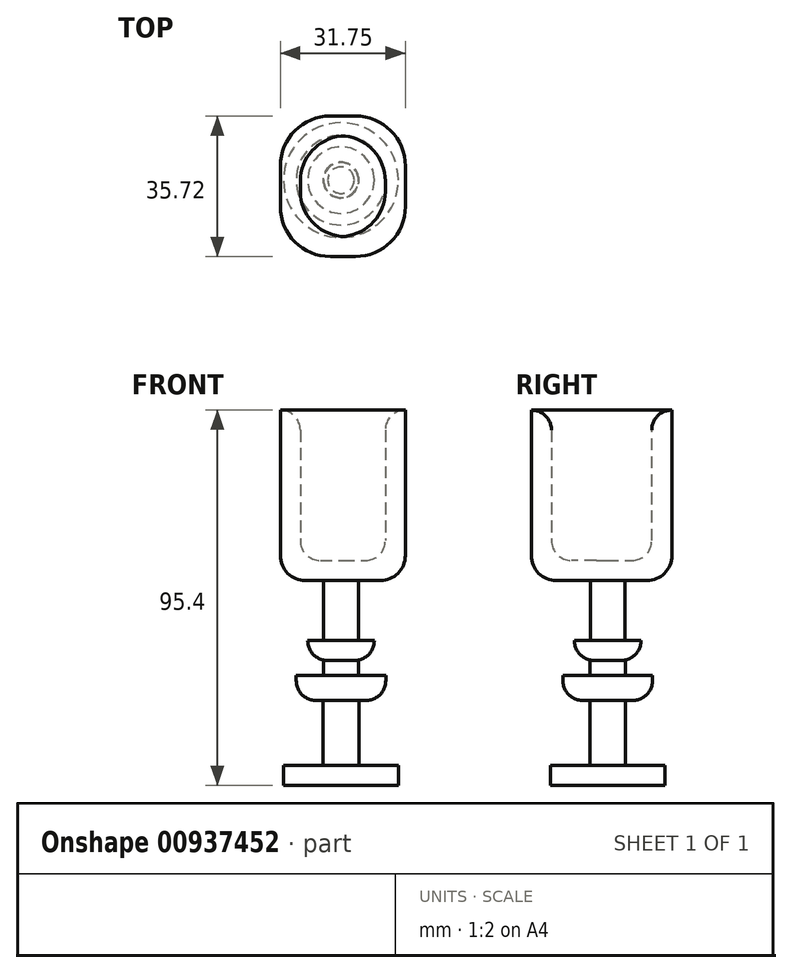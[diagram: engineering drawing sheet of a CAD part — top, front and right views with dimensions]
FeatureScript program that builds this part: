
annotation { "Feature Type Name" : "Feature", "Feature Type Description" : "" }
export const myFeature = defineFeature(function(context is Context, id is Id, definition is map)
    precondition{}
    {
        {
            var Q0;
            Q0=qCreatedBy(makeId("Right.planeOp"),FACE);
            var sketch = newSketch(context, id + "F0", { "sketchPlane" : qUnion([Q0])});
            skLineSegment(sketch, "E0.bottom", {"start": v(-15.73, 59.27) * mm, "end": v(19.99, 59.27) * mm});
            skLineSegment(sketch, "E0.top", {"start": v(-15.73, 15.94) * mm, "end": v(19.99, 15.94) * mm});
            skLineSegment(sketch, "E0.left", {"start": v(-15.73, 59.27) * mm, "end": v(-15.73, 15.94) * mm});
            skLineSegment(sketch, "E0.right", {"start": v(19.99, 59.27) * mm, "end": v(19.99, 15.94) * mm});
            skPoint(sketch, "E0.middle", {"position": v(2.13, 37.6) * mm});
            skSolve(sketch);
        }
        {
            var Q0;
            Q0 = qSketchRegion(id + "F0", true);
            extrude(context, id + "F1", {"entities" : qUnion([Q0]), "depth" : 31.75 * mm, "offsetDistance" : 25.4 * mm});
        }
        {
            var Q0;
            Q0=makeQuery(id+"F1.opExtrude","SWEPT_FACE",FACE,{"disambiguationData":[OSD([sQuery(id+"F0.wireOp",EDGE,"E0.bottom")])]});
            shell(context, id + "F2", {"entities" : qUnion([Q0]), "thickness" : 5.08 * mm});
        }
        {
            var Q0;
            Q0=makeQuery(id+"F1.opExtrude","CAP_EDGE",EDGE,{"disambiguationData":[OSD([sQuery(id+"F0.wireOp",EDGE,"E0.left")])],"isStart":true});
            var Q1;
            Q1=makeQuery(id+"F1.opExtrude","CAP_EDGE",EDGE,{"disambiguationData":[OSD([sQuery(id+"F0.wireOp",EDGE,"E0.left")])],"isStart":false});
            var Q2;
            Q2=makeQuery(id+"F1.opExtrude","CAP_EDGE",EDGE,{"disambiguationData":[OSD([sQuery(id+"F0.wireOp",EDGE,"E0.right")])],"isStart":false});
            var Q3;
            Q3=makeQuery(id+"F1.opExtrude","CAP_EDGE",EDGE,{"disambiguationData":[OSD([sQuery(id+"F0.wireOp",EDGE,"E0.right")])],"isStart":true});
            fillet(context, id + "F3", {"entities" : qUnion([Q0, Q1, Q2, Q3]), "radius" : 12.7 * mm, "tangentPropagation" : true, "allowEdgeOverflow" : false});
        }
        {
            var Q0;
            {var subQ0=sQuery(id+"F0.wireOp",EDGE,"E0.left");Q0=makeQuery(id+"F2.opShell","OFFSET_EDGE",EDGE,{"disambiguationData":[OSD([subQ0]),TDD([makeQuery(id+"F1.opExtrude","CAP_EDGE",EDGE,{"disambiguationData":[OSD([subQ0])],"isStart":true})])]});}
            var Q1;
            {var subQ0=sQuery(id+"F0.wireOp",EDGE,"E0.right");Q1=makeQuery(id+"F2.opShell","OFFSET_EDGE",EDGE,{"disambiguationData":[OSD([subQ0]),TDD([makeQuery(id+"F1.opExtrude","CAP_EDGE",EDGE,{"disambiguationData":[OSD([subQ0])],"isStart":true})])]});}
            var Q2;
            {var subQ0=sQuery(id+"F0.wireOp",EDGE,"E0.right");Q2=makeQuery(id+"F2.opShell","OFFSET_EDGE",EDGE,{"disambiguationData":[OSD([subQ0]),TDD([makeQuery(id+"F1.opExtrude","CAP_EDGE",EDGE,{"disambiguationData":[OSD([subQ0])],"isStart":false})])]});}
            var Q3;
            {var subQ0=sQuery(id+"F0.wireOp",EDGE,"E0.left");Q3=makeQuery(id+"F2.opShell","OFFSET_EDGE",EDGE,{"disambiguationData":[OSD([subQ0]),TDD([makeQuery(id+"F1.opExtrude","CAP_EDGE",EDGE,{"disambiguationData":[OSD([subQ0])],"isStart":false})])]});}
            fillet(context, id + "F4", {"entities" : qUnion([Q0, Q1, Q2, Q3]), "radius" : 11.43 * mm, "tangentPropagation" : true, "allowEdgeOverflow" : false});
        }
        {
            var Q0;
            Q0=makeQuery(id+"F1.opExtrude","SWEPT_EDGE",EDGE,{"disambiguationData":[OSD([sQuery(id+"F0.wireOp",EDGE,"E0.top"),sQuery(id+"F0.wireOp",EDGE,"E0.left")])]});
            var Q1;
            Q1=makeQuery(id+"F3.opFillet","BLEND_EDGE",EDGE,{"blendedFrom":[makeQuery(id+"F1.opExtrude","CAP_EDGE",EDGE,{"disambiguationData":[OSD([sQuery(id+"F0.wireOp",EDGE,"E0.left")])],"isStart":true}),makeQuery(id+"F1.opExtrude","SWEPT_FACE",FACE,{"disambiguationData":[OSD([sQuery(id+"F0.wireOp",EDGE,"E0.top")])]})],"blendedInto":[makeQuery(id+"F1.opExtrude","SWEPT_FACE",FACE,{"disambiguationData":[OSD([sQuery(id+"F0.wireOp",EDGE,"E0.top")])]})]});
            var Q2;
            Q2=makeQuery(id+"F1.opExtrude","CAP_EDGE",EDGE,{"disambiguationData":[OSD([sQuery(id+"F0.wireOp",EDGE,"E0.top")])],"isStart":true});
            var Q3;
            Q3=makeQuery(id+"F3.opFillet","BLEND_EDGE",EDGE,{"blendedFrom":[makeQuery(id+"F1.opExtrude","CAP_EDGE",EDGE,{"disambiguationData":[OSD([sQuery(id+"F0.wireOp",EDGE,"E0.right")])],"isStart":true}),makeQuery(id+"F1.opExtrude","SWEPT_FACE",FACE,{"disambiguationData":[OSD([sQuery(id+"F0.wireOp",EDGE,"E0.top")])]})],"blendedInto":[makeQuery(id+"F1.opExtrude","SWEPT_FACE",FACE,{"disambiguationData":[OSD([sQuery(id+"F0.wireOp",EDGE,"E0.top")])]})]});
            var Q4;
            Q4=makeQuery(id+"F1.opExtrude","SWEPT_EDGE",EDGE,{"disambiguationData":[OSD([sQuery(id+"F0.wireOp",EDGE,"E0.top"),sQuery(id+"F0.wireOp",EDGE,"E0.right")])]});
            var Q5;
            Q5=makeQuery(id+"F3.opFillet","BLEND_EDGE",EDGE,{"blendedFrom":[makeQuery(id+"F1.opExtrude","CAP_EDGE",EDGE,{"disambiguationData":[OSD([sQuery(id+"F0.wireOp",EDGE,"E0.right")])],"isStart":false}),makeQuery(id+"F1.opExtrude","SWEPT_FACE",FACE,{"disambiguationData":[OSD([sQuery(id+"F0.wireOp",EDGE,"E0.top")])]})],"blendedInto":[makeQuery(id+"F1.opExtrude","SWEPT_FACE",FACE,{"disambiguationData":[OSD([sQuery(id+"F0.wireOp",EDGE,"E0.top")])]})]});
            var Q6;
            Q6=makeQuery(id+"F1.opExtrude","CAP_EDGE",EDGE,{"disambiguationData":[OSD([sQuery(id+"F0.wireOp",EDGE,"E0.top")])],"isStart":false});
            var Q7;
            Q7=makeQuery(id+"F3.opFillet","BLEND_EDGE",EDGE,{"blendedFrom":[makeQuery(id+"F1.opExtrude","CAP_EDGE",EDGE,{"disambiguationData":[OSD([sQuery(id+"F0.wireOp",EDGE,"E0.left")])],"isStart":false}),makeQuery(id+"F1.opExtrude","SWEPT_FACE",FACE,{"disambiguationData":[OSD([sQuery(id+"F0.wireOp",EDGE,"E0.top")])]})],"blendedInto":[makeQuery(id+"F1.opExtrude","SWEPT_FACE",FACE,{"disambiguationData":[OSD([sQuery(id+"F0.wireOp",EDGE,"E0.top")])]})]});
            fillet(context, id + "F5", {"entities" : qUnion([Q0, Q1, Q2, Q3, Q4, Q5, Q6, Q7]), "radius" : 6.35 * mm, "tangentPropagation" : true, "allowEdgeOverflow" : false});
        }
        {
            var Q0;
            {var subQ0=sQuery(id+"F0.wireOp",EDGE,"E0.right");Q0=makeQuery(id+"F4.opFillet","BLEND_FACE",FACE,{"disambiguationData":[OSD([subQ0]),TDD([makeQuery(id+"F2.opShell","OFFSET_EDGE",EDGE,{"disambiguationData":[OSD([subQ0]),TDD([makeQuery(id+"F1.opExtrude","CAP_EDGE",EDGE,{"disambiguationData":[OSD([subQ0])],"isStart":false})])]})])]});}
            var Q1;
            {var subQ0=sQuery(id+"F0.wireOp",EDGE,"E0.left");Q1=makeQuery(id+"F4.opFillet","BLEND_FACE",FACE,{"disambiguationData":[OSD([subQ0]),TDD([makeQuery(id+"F2.opShell","OFFSET_EDGE",EDGE,{"disambiguationData":[OSD([subQ0]),TDD([makeQuery(id+"F1.opExtrude","CAP_EDGE",EDGE,{"disambiguationData":[OSD([subQ0])],"isStart":false})])]})])]});}
            var Q2;
            {var subQ0=sQuery(id+"F0.wireOp",EDGE,"E0.right");Q2=makeQuery(id+"F4.opFillet","BLEND_FACE",FACE,{"disambiguationData":[OSD([subQ0]),TDD([makeQuery(id+"F2.opShell","OFFSET_EDGE",EDGE,{"disambiguationData":[OSD([subQ0]),TDD([makeQuery(id+"F1.opExtrude","CAP_EDGE",EDGE,{"disambiguationData":[OSD([subQ0])],"isStart":true})])]})])]});}
            var Q3;
            {var subQ0=sQuery(id+"F0.wireOp",EDGE,"E0.left");Q3=makeQuery(id+"F4.opFillet","BLEND_FACE",FACE,{"disambiguationData":[OSD([subQ0]),TDD([makeQuery(id+"F2.opShell","OFFSET_EDGE",EDGE,{"disambiguationData":[OSD([subQ0]),TDD([makeQuery(id+"F1.opExtrude","CAP_EDGE",EDGE,{"disambiguationData":[OSD([subQ0])],"isStart":true})])]})])]});}
            fillet(context, id + "F6", {"entities" : qUnion([Q0, Q1, Q2, Q3]), "radius" : 5.08 * mm, "tangentPropagation" : true, "allowEdgeOverflow" : false});
        }
        {
            var Q0;
            Q0=makeQuery(id+"F1.opExtrude","SWEPT_FACE",FACE,{"disambiguationData":[OSD([sQuery(id+"F0.wireOp",EDGE,"E0.top")])]});
            var sketch = newSketch(context, id + "F7", { "sketchPlane" : qUnion([Q0])});
            skCircle(sketch, "E1", {"center": v(15.41, -3.7) * mm, "radius": 4.43 * mm});
            skSolve(sketch);
        }
        {
            var Q0;
            Q0 = qSketchRegion(id + "F7", true);
            extrude(context, id + "F8", {"entities" : qUnion([Q0]), "operationType" : NewBodyOperationType.ADD, "depth" : 15.24 * mm, "offsetDistance" : 25.4 * mm});
        }
        {
            var Q0;
            Q0=makeQuery(id+"F8.opExtrude","CAP_FACE",FACE,{"disambiguationData":[OSD([sQuery(id+"F7.wireOp",EDGE,"E1")])],"isStart":false});
            var sketch = newSketch(context, id + "F9", { "sketchPlane" : qUnion([Q0])});
            skCircle(sketch, "E2", {"center": v(15.41, -3.7) * mm, "radius": 8.45 * mm});
            skSolve(sketch);
        }
        {
            var Q0;
            Q0 = qSketchRegion(id + "F9", true);
            extrude(context, id + "F10", {"entities" : qUnion([Q0]), "operationType" : NewBodyOperationType.ADD, "depth" : 5.08 * mm, "offsetDistance" : 25.4 * mm});
        }
        {
            var Q0;
            Q0=makeQuery(id+"F10.opExtrude","CAP_EDGE",EDGE,{"disambiguationData":[OSD([sQuery(id+"F9.wireOp",EDGE,"E2")])],"isStart":false});
            fillet(context, id + "F11", {"entities" : qUnion([Q0]), "radius" : 5.08 * mm, "tangentPropagation" : true, "allowEdgeOverflow" : false});
        }
        {
            var Q0;
            Q0=makeQuery(id+"F10.opExtrude","CAP_FACE",FACE,{"disambiguationData":[OSD([sQuery(id+"F9.wireOp",EDGE,"E2")])],"isStart":false});
            var sketch = newSketch(context, id + "F12", { "sketchPlane" : qUnion([Q0])});
            skCircle(sketch, "E3", {"center": v(15.41, -3.7) * mm, "radius": 4.45 * mm});
            skSolve(sketch);
        }
        {
            var Q0;
            Q0 = qSketchRegion(id + "F12", true);
            extrude(context, id + "F13", {"entities" : qUnion([Q0]), "operationType" : NewBodyOperationType.ADD, "depth" : 3.8 * mm, "offsetDistance" : 25.4 * mm});
        }
        {
            var Q0;
            Q0=makeQuery(id+"F13.opExtrude","CAP_FACE",FACE,{"disambiguationData":[OSD([sQuery(id+"F12.wireOp",EDGE,"E3")])],"isStart":false});
            var sketch = newSketch(context, id + "F14", { "sketchPlane" : qUnion([Q0])});
            skCircle(sketch, "E4", {"center": v(15.41, -3.7) * mm, "radius": 11.37 * mm});
            skSolve(sketch);
        }
        {
            var Q0;
            Q0 = qSketchRegion(id + "F14", true);
            extrude(context, id + "F15", {"entities" : qUnion([Q0]), "operationType" : NewBodyOperationType.ADD, "depth" : 6.35 * mm, "offsetDistance" : 25.4 * mm});
        }
        {
            var Q0;
            Q0=makeQuery(id+"F15.opExtrude","CAP_EDGE",EDGE,{"disambiguationData":[OSD([sQuery(id+"F14.wireOp",EDGE,"E4")])],"isStart":false});
            fillet(context, id + "F16", {"entities" : qUnion([Q0]), "radius" : 5.08 * mm, "tangentPropagation" : true, "allowEdgeOverflow" : false});
        }
        {
            var Q0;
            Q0=makeQuery(id+"F15.opExtrude","CAP_FACE",FACE,{"disambiguationData":[OSD([sQuery(id+"F14.wireOp",EDGE,"E4")])],"isStart":false});
            var sketch = newSketch(context, id + "F17", { "sketchPlane" : qUnion([Q0])});
            skCircle(sketch, "E5", {"center": v(15.41, -3.7) * mm, "radius": 4.55 * mm});
            skSolve(sketch);
        }
        {
            var Q0;
            Q0 = qSketchRegion(id + "F17", true);
            extrude(context, id + "F18", {"entities" : qUnion([Q0]), "operationType" : NewBodyOperationType.ADD, "depth" : 16.5 * mm, "offsetDistance" : 25.4 * mm});
        }
        {
            var Q0;
            Q0=makeQuery(id+"F18.opExtrude","CAP_FACE",FACE,{"disambiguationData":[OSD([sQuery(id+"F17.wireOp",EDGE,"E5")])],"isStart":false});
            var sketch = newSketch(context, id + "F19", { "sketchPlane" : qUnion([Q0])});
            skCircle(sketch, "E6", {"center": v(15.41, -3.7) * mm, "radius": 14.59 * mm});
            skSolve(sketch);
        }
        {
            var Q0;
            Q0 = qSketchRegion(id + "F19", true);
            extrude(context, id + "F20", {"entities" : qUnion([Q0]), "operationType" : NewBodyOperationType.ADD, "depth" : 5.08 * mm, "offsetDistance" : 25.4 * mm});
        }
    });
